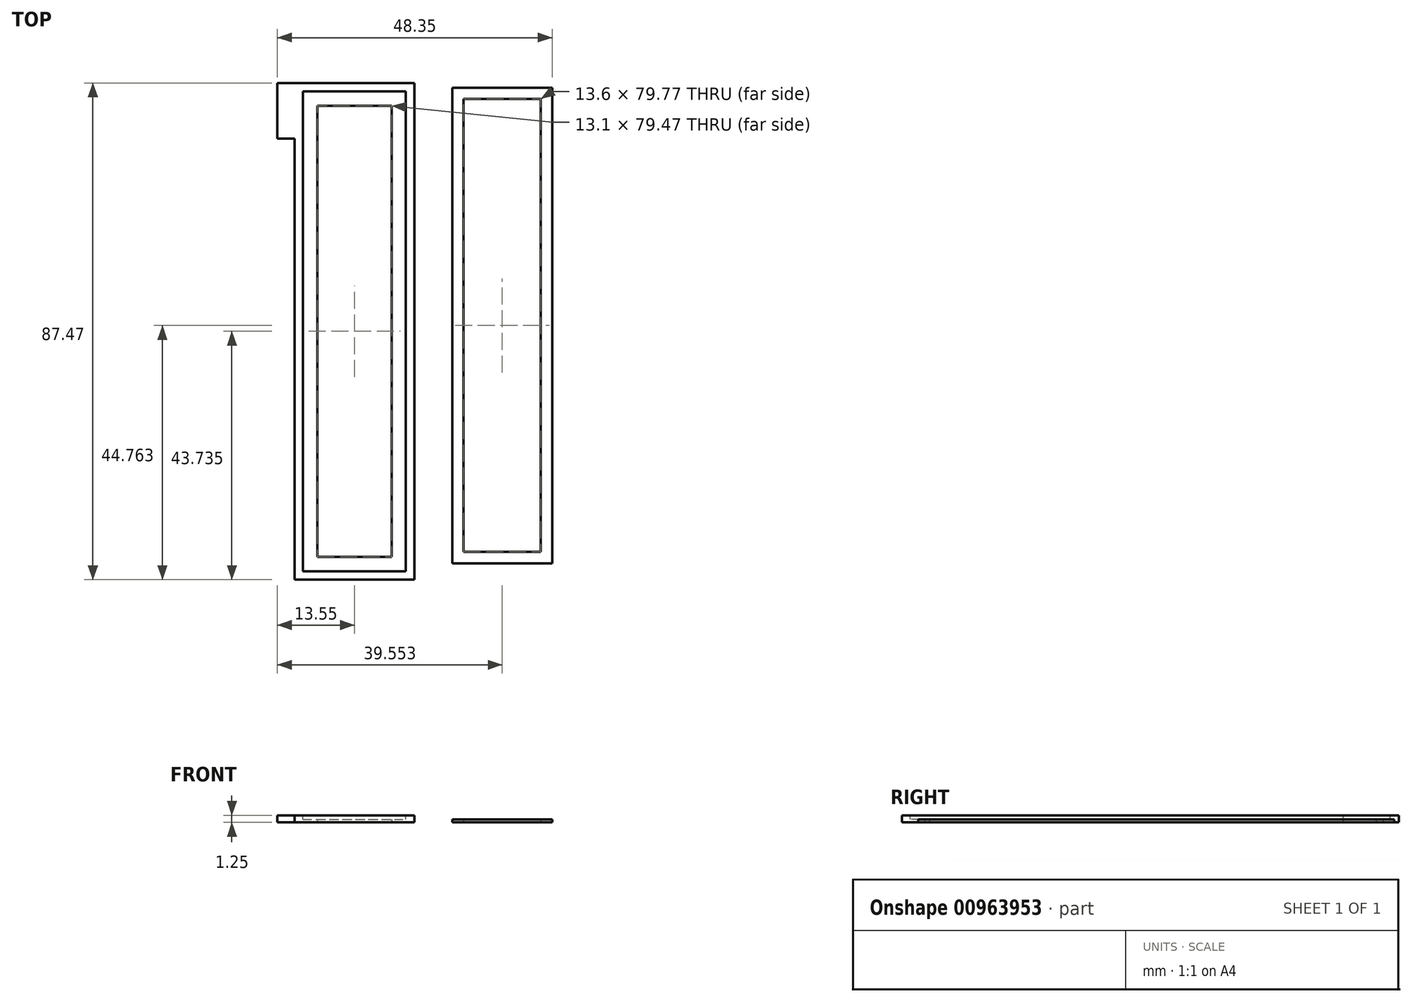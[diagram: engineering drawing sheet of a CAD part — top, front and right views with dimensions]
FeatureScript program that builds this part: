
annotation { "Feature Type Name" : "Feature", "Feature Type Description" : "" }
export const myFeature = defineFeature(function(context is Context, id is Id, definition is map)
    precondition{}
    {
        {
            var Q0;
            Q0=qCreatedBy(makeId("Top.planeOp"),FACE);
            var sketch = newSketch(context, id + "F0", { "sketchPlane" : qUnion([Q0])});
            skLineSegment(sketch, "E0.bottom", {"start": v(0, 0) * mm, "end": v(21.1, 0) * mm});
            skLineSegment(sketch, "E0.top", {"start": v(0, 87.47) * mm, "end": v(21.1, 87.47) * mm});
            skLineSegment(sketch, "E0.left", {"start": v(0, 0) * mm, "end": v(0, 87.47) * mm});
            skLineSegment(sketch, "E0.right", {"start": v(21.1, 0) * mm, "end": v(21.1, 87.47) * mm});
            skLineSegment(sketch, "E1.bottom", {"start": v(4, 83.47) * mm, "end": v(17.1, 83.47) * mm});
            skLineSegment(sketch, "E1.top", {"start": v(4, 4) * mm, "end": v(17.1, 4) * mm});
            skLineSegment(sketch, "E1.left", {"start": v(4, 83.47) * mm, "end": v(4, 4) * mm});
            skLineSegment(sketch, "E1.right", {"start": v(17.1, 83.47) * mm, "end": v(17.1, 4) * mm});
            skSolve(sketch);
        }
        {
            var Q0;
            Q0=qSketchRegion(id+"F0",true);
            extrude(context, id + "F1", {"entities" : qUnion([Q0]), "depth" : 1.25 * mm, "offsetDistance" : 25 * mm});
        }
        {
            var Q0;
            Q0=makeQuery(id+"F1.opExtrude","CAP_FACE",FACE,{"disambiguationData":[OSD([sQuery(id+"F0.wireOp",EDGE,"E0.bottom"),sQuery(id+"F0.wireOp",EDGE,"E0.top"),sQuery(id+"F0.wireOp",EDGE,"E0.left"),sQuery(id+"F0.wireOp",EDGE,"E0.right"),sQuery(id+"F0.wireOp",EDGE,"E1.bottom"),sQuery(id+"F0.wireOp",EDGE,"E1.top"),sQuery(id+"F0.wireOp",EDGE,"E1.left"),sQuery(id+"F0.wireOp",EDGE,"E1.right")])],"isStart":false});
            var sketch = newSketch(context, id + "F2", { "sketchPlane" : qUnion([Q0])});
            skLineSegment(sketch, "E2.bottom", {"start": v(1.5, 85.97) * mm, "end": v(19.6, 85.97) * mm});
            skLineSegment(sketch, "E2.top", {"start": v(1.5, 1.5) * mm, "end": v(19.6, 1.5) * mm});
            skLineSegment(sketch, "E2.left", {"start": v(1.5, 85.97) * mm, "end": v(1.5, 1.5) * mm});
            skLineSegment(sketch, "E2.right", {"start": v(19.6, 85.97) * mm, "end": v(19.6, 1.5) * mm});
            skSolve(sketch);
        }
        {
            var Q0;
            Q0 = qSketchRegion(id + "F2", true);
            extrude(context, id + "F3", {"entities" : qUnion([Q0]), "operationType" : NewBodyOperationType.REMOVE, "oppositeDirection" : true, "depth" : 0.75 * mm, "offsetDistance" : 25 * mm});
        }
        {
            var Q0;
            Q0=qCreatedBy(makeId("Top.planeOp"),FACE);
            var sketch = newSketch(context, id + "F4", { "sketchPlane" : qUnion([Q0])});
            skLineSegment(sketch, "E3.bottom", {"start": v(27.75, 86.65) * mm, "end": v(45.35, 86.65) * mm});
            skLineSegment(sketch, "E3.top", {"start": v(27.75, 2.88) * mm, "end": v(45.35, 2.88) * mm});
            skLineSegment(sketch, "E3.left", {"start": v(27.75, 86.65) * mm, "end": v(27.75, 2.88) * mm});
            skLineSegment(sketch, "E3.right", {"start": v(45.35, 86.65) * mm, "end": v(45.35, 2.88) * mm});
            skLineSegment(sketch, "E4.bottom", {"start": v(29.75, 84.65) * mm, "end": v(43.35, 84.65) * mm});
            skLineSegment(sketch, "E4.top", {"start": v(29.75, 4.88) * mm, "end": v(43.35, 4.88) * mm});
            skLineSegment(sketch, "E4.left", {"start": v(29.75, 84.65) * mm, "end": v(29.75, 4.88) * mm});
            skLineSegment(sketch, "E4.right", {"start": v(43.35, 84.65) * mm, "end": v(43.35, 4.88) * mm});
            skSolve(sketch);
        }
        {
            var Q0;
            Q0 = qSketchRegion(id + "F4", true);
            extrude(context, id + "F5", {"entities" : qUnion([Q0]), "depth" : 0.5 * mm, "offsetDistance" : 25 * mm});
        }
        {
            var Q0;
            Q0=makeQuery(id+"F1.opExtrude","SWEPT_FACE",FACE,{"disambiguationData":[OSD([sQuery(id+"F0.wireOp",EDGE,"E0.left")])]});
            var sketch = newSketch(context, id + "F6", { "sketchPlane" : qUnion([Q0])});
            skLineSegment(sketch, "E5.bottom", {"start": v(-87.47, 0) * mm, "end": v(-77.67, 0) * mm});
            skLineSegment(sketch, "E5.top", {"start": v(-87.47, 1.25) * mm, "end": v(-77.67, 1.25) * mm});
            skLineSegment(sketch, "E5.left", {"start": v(-87.47, 0) * mm, "end": v(-87.47, 1.25) * mm});
            skLineSegment(sketch, "E5.right", {"start": v(-77.67, 0) * mm, "end": v(-77.67, 1.25) * mm});
            skSolve(sketch);
        }
        {
            var Q0;
            Q0 = qSketchRegion(id + "F6", true);
            extrude(context, id + "F7", {"entities" : qUnion([Q0]), "operationType" : NewBodyOperationType.ADD, "depth" : 3 * mm, "offsetDistance" : 25 * mm});
        }
    });
